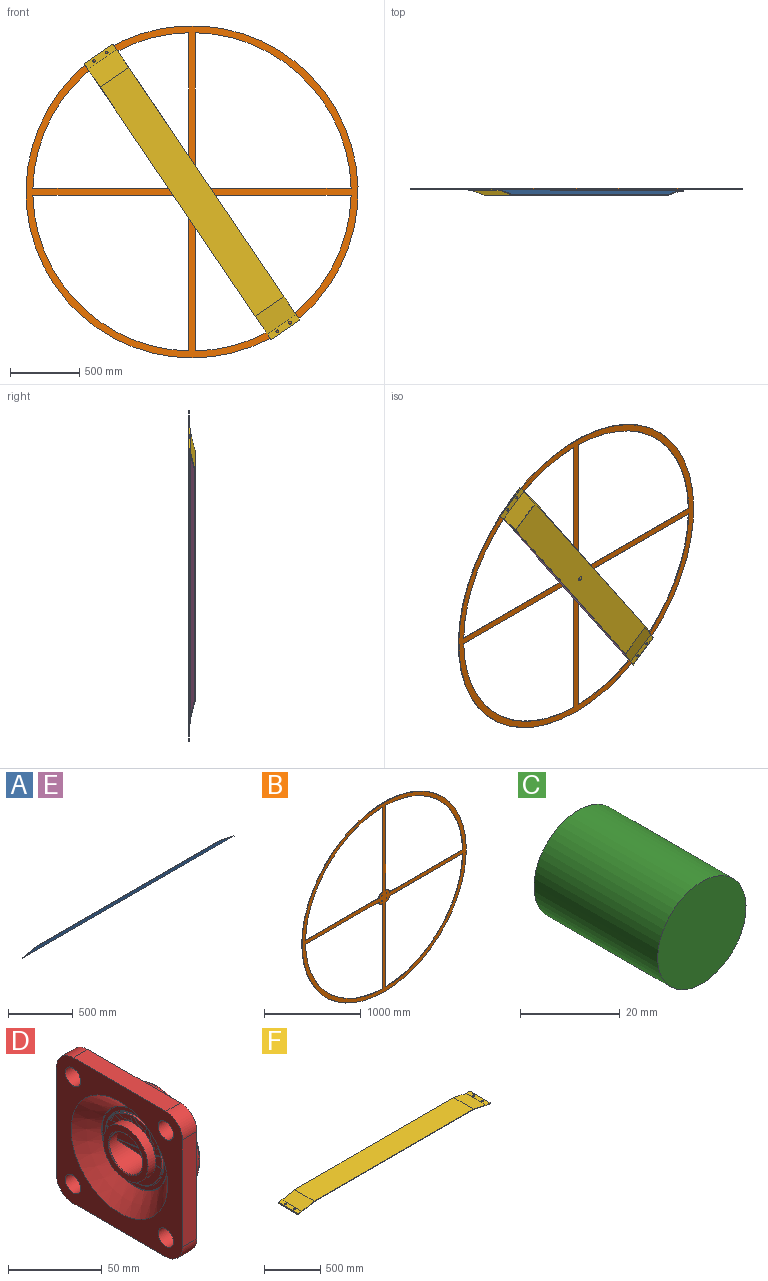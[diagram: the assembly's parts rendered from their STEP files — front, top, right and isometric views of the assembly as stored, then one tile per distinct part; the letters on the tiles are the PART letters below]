
ASSEMBLY  parts=6 mates=5
PART A: 6 faces, bbox 2310x5x33 mm
  f0: plane 155x33mm, normal (0.21,0,0.98), area 792.4mm2, adj f1,f3,f4,f5
  f1: plane 2000x5mm, normal (0,0,1), area 10000mm2, adj f0,f2,f4,f5
  f2: plane 155x33mm, normal (-0.21,0,0.98), area 792.4mm2, adj f1,f3,f4,f5
  f3: plane 2310x5mm, normal (0,0,-1), area 11550mm2, adj f0,f2,f4,f5
  f4: plane 2310x33mm, normal (0,-1,0), area 71115mm2, adj f0,f1,f2,f3
  f5: plane 2310x33mm, normal (0,1,0), area 71115mm2, adj f0,f1,f2,f3
PART B: 31 faces, bbox 2400x5x2400 mm
  f0: cylinder r=1150mm len=1124.73mm, axis (0,1,0), area 8782.1mm2, adj f1,f24,f29,f30
  f1: plane 1074.73x5mm, normal (1,0,0), area 5373.6mm2, adj f0,f2,f29,f30
  f2: plane 10.63x5mm, normal (0,0,-1), area 53.1mm2, adj f1,f3,f29,f30
  f3: cylinder r=45mm len=39.37mm, axis (0,1,0), area 300.2mm2, adj f2,f4,f29,f30
  f4: plane 10.63x5mm, normal (1,0,0), area 53.1mm2, adj f3,f24,f29,f30
  f5: plane 1074.73x5mm, normal (1,0,0), area 5373.6mm2, adj f6,f25,f29,f30
  f6: cylinder r=1150mm len=1124.73mm, axis (0,1,0), area 8782.1mm2, adj f5,f7,f29,f30
  f7: plane 1074.73x5mm, normal (0,0,1), area 5373.6mm2, adj f6,f8,f29,f30
  f8: plane 10.63x5mm, normal (1,0,0), area 53.1mm2, adj f7,f9,f29,f30
  f9: cylinder r=45mm len=39.37mm, axis (0,1,0), area 300.2mm2, adj f8,f25,f29,f30
  f10: plane 1074.73x5mm, normal (0,0,1), area 5373.6mm2, adj f11,f26,f29,f30
  f11: cylinder r=1150mm len=1124.73mm, axis (0,1,0), area 8782.1mm2, adj f10,f12,f29,f30
  f12: plane 1074.73x5mm, normal (-1,0,0), area 5373.6mm2, adj f11,f13,f29,f30
  f13: plane 10.63x5mm, normal (0,0,1), area 53.1mm2, adj f12,f14,f29,f30
  f14: cylinder r=45mm len=39.37mm, axis (0,1,0), area 300.2mm2, adj f13,f26,f29,f30
  f15: cylinder r=1150mm len=1124.73mm, axis (0,1,0), area 8782.1mm2, adj f16,f27,f29,f30
  f16: plane 1074.73x5mm, normal (0,0,-1), area 5373.6mm2, adj f15,f17,f29,f30
  f17: plane 10.63x5mm, normal (-1,0,0), area 53.1mm2, adj f16,f18,f29,f30
  f18: cylinder r=45mm len=39.37mm, axis (0,1,0), area 300.2mm2, adj f17,f19,f29,f30
  f19: plane 10.63x5mm, normal (0,0,-1), area 53.1mm2, adj f18,f27,f29,f30
  f20: cylinder r=5.5mm len=11mm, axis (0,1,0), area 172.8mm2, adj f29,f30
  f21: cylinder r=5.5mm len=11mm, axis (0,1,0), area 172.8mm2, adj f29,f30
  f22: cylinder r=5.5mm len=11mm, axis (0,1,0), area 172.8mm2, adj f29,f30
  f23: cylinder r=1200mm len=2400mm, axis (0,1,0), area 37699.1mm2, adj f29,f30
  f24: plane 1074.73x5mm, normal (0,0,-1), area 5373.6mm2, adj f0,f4,f29,f30
  f25: plane 10.63x5mm, normal (0,0,1), area 53.1mm2, adj f5,f9,f29,f30
  f26: plane 10.63x5mm, normal (-1,0,0), area 53.1mm2, adj f10,f14,f29,f30
  f27: plane 1074.73x5mm, normal (-1,0,0), area 5373.6mm2, adj f15,f19,f29,f30
  f28: cylinder r=5.5mm len=11mm, axis (0,1,0), area 172.8mm2, adj f29,f30
  f29: plane 2400x2400mm, normal (0,-1,0), area 604604.7mm2, adj f0,f1,f2,f3,f4,f5,f6,f7
  f30: plane 2400x2400mm, normal (0,1,0), area 604604.7mm2, adj f0,f1,f2,f3,f4,f5,f6,f7
PART C: 3 faces, bbox 25x35x25 mm
  f0: cylinder r=12.5mm len=35mm, axis (0,1,0), area 2748.9mm2, adj f1,f2
  f1: plane 25x25mm, normal (0,-1,0), area 490.9mm2, adj f0
  f2: plane 25x25mm, normal (0,1,0), area 490.9mm2, adj f0
PART D: 78 faces, bbox 52x95x95 mm
  f0: plane 2.89x2.17mm, normal (0,-0.5,0.87), area 5.4mm2, adj f2,f3,f4,f5,f6,f7
  f1: plane 2.89x2.5mm, normal (0,1,0), area 5.4mm2, adj f8,f9,f10,f11,f12,f13
  f2: plane 1.77x1.74mm, normal (0.87,0.43,0.25), area 1.9mm2, adj f0,f3,f7,f14
  f3: plane 1.44x1.14mm, normal (0,0.87,0.5), area 1.9mm2, adj f0,f2,f4,f14
  f4: plane 1.77x1.74mm, normal (-0.87,0.43,0.25), area 1.9mm2, adj f0,f3,f5,f14
  f5: plane 1.77x1.74mm, normal (-0.87,-0.43,-0.25), area 1.9mm2, adj f0,f4,f6,f14
  f6: plane 1.44x1.14mm, normal (0,-0.87,-0.5), area 1.9mm2, adj f0,f5,f7,f14
  f7: plane 1.77x1.74mm, normal (0.87,-0.43,-0.25), area 1.9mm2, adj f0,f2,f6,f14
  f8: plane 1.32x1.25mm, normal (0.5,0,0.87), area 1.9mm2, adj f1,f9,f13,f15
  f9: plane 1.44x1.32mm, normal (1,0,0), area 1.9mm2, adj f1,f8,f10,f15
  f10: plane 1.32x1.25mm, normal (0.5,0,-0.87), area 1.9mm2, adj f1,f9,f11,f15
  f11: plane 1.32x1.25mm, normal (-0.5,0,-0.87), area 1.9mm2, adj f1,f10,f12,f15
  f12: plane 1.44x1.32mm, normal (-1,0,0), area 1.9mm2, adj f1,f11,f13,f15
  f13: plane 1.32x1.25mm, normal (-0.5,0,0.87), area 1.9mm2, adj f1,f8,f12,f15
  f14: plane 5.09x4.33mm, normal (0,-0.5,0.87), area 14.2mm2, adj f2,f3,f4,f5,f6,f7,f16
  f15: plane 5.09x5mm, normal (0,1,0), area 14.2mm2, adj f8,f9,f10,f11,f12,f13,f17
  f16: cylinder r=2.5mm len=5mm, axis (0,0.5,-0.87), area 14.2mm2, adj f14,f18
  f17: cylinder r=2.5mm len=5mm, axis (0,-1,0), area 14.2mm2, adj f15,f18
  f18: cylinder r=16.9mm len=33.8mm, axis (-1,0,0), area 1176.5mm2, adj f16,f17,f19,f20
  f19: plane 43.29x42.5mm, normal (1,0,0), area 521.4mm2, adj f18,f21
  f20: plane 34.43x33.8mm, normal (1,0,0), area 366.3mm2, adj f18,f22
  f21: cylinder r=21.25mm len=42.5mm, axis (-1,0,0), area 166.9mm2, adj f19,f23
  f22: torus R=13mm, axis (-1,0,0), area 62.6mm2, adj f20,f24
  f23: plane 44.97x44.16mm, normal (1,0,0), area 112.7mm2, adj f21,f25
  f24: cylinder r=12.5mm len=33.1mm, axis (-1,0,0), area 2599.7mm2, adj f22,f26
  f25: cylinder r=22.08mm len=44.16mm, axis (-1,0,0), area 55.5mm2, adj f23,f27
  f26: torus R=13mm, axis (-1,0,0), area 62.6mm2, adj f24,f28
  f27: plane 49.5x49.04mm, normal (1,0,0), area 357.5mm2, adj f25,f29
  f28: plane 34.43x33.8mm, normal (-1,0,0), area 366.3mm2, adj f26,f30
  f29: torus R=24.52mm, axis (-1,0,0), area 100.7mm2, adj f27,f31
  f30: cylinder r=16.9mm len=33.8mm, axis (-1,0,0), area 631.8mm2, adj f28,f32
  f31: sphere r=26mm, area 64.7mm2, adj f29,f33
  f32: plane 43.29x42.5mm, normal (-1,0,0), area -733.9mm2, adj f30,f35
  f33: cone r=25.12mm half-angle=10deg, axis (1,0,0), area 402.3mm2, adj f31,f36
  f34: sphere r=26mm, area 0mm2, adj f37
  f35: cylinder r=21.25mm len=42.5mm, axis (-1,0,0), area 166.9mm2, adj f32,f38
  f36: plane 61.85x61.29mm, normal (1,0,0), area 932.4mm2, adj f33,f39
  f37: cylinder r=4.29mm len=10.68mm, axis (-0.26,-0.97,0), area 213.4mm2, adj f34,f40
  f38: plane 44.97x44.16mm, normal (-1,0,0), area -1650.4mm2, adj f35,f41
  f39: torus R=30.64mm, axis (-1,0,0), area 522.5mm2, adj f36,f40,f42
  f40: cone r=5.07mm half-angle=45deg, axis (0.26,0.97,0), area 17mm2, adj f37,f39,f42
  f41: cylinder r=22.08mm len=44.16mm, axis (-1,0,0), area 55.5mm2, adj f38,f43
  f42: cone r=34.59mm half-angle=15deg, axis (-1,0,0), area 3314mm2, adj f39,f40,f44
  f43: plane 49.5x49.04mm, normal (-1,0,0), area 357.5mm2, adj f41,f45
  f44: torus R=38.53mm, axis (-1,0,0), area 615.2mm2, adj f42,f46
  f45: torus R=24.52mm, axis (-1,0,0), area 100.7mm2, adj f43,f47
  f46: plane 95x95mm, normal (1,0,0), area 3810.4mm2, adj f44,f48,f49,f50,f51,f52,f53,f54
  f47: sphere r=26mm, area 59.3mm2, adj f45,f60
  f48: cylinder r=5.75mm len=11.5mm, axis (-1,0,0), area 397.4mm2, adj f46,f61
  f49: cylinder r=5.75mm len=11.5mm, axis (-1,0,0), area 397.4mm2, adj f46,f61
  f50: cylinder r=5.75mm len=11.5mm, axis (-1,0,0), area 397.4mm2, adj f46,f61
  f51: cylinder r=5.75mm len=11.5mm, axis (-1,0,0), area 397.4mm2, adj f46,f61
  f52: plane 70x11mm, normal (0,1,0), area 770mm2, adj f46,f53,f59,f61
  f53: cylinder r=12.5mm len=12.5mm, axis (-1,0,0), area 216mm2, adj f46,f52,f54,f61
  f54: plane 70x11mm, normal (0,0,-1), area 770mm2, adj f46,f53,f55,f61
  f55: cylinder r=12.5mm len=12.5mm, axis (-1,0,0), area 216mm2, adj f46,f54,f56,f61
  f56: plane 70x11mm, normal (0,-1,0), area 770mm2, adj f46,f55,f57,f61
  f57: cylinder r=12.5mm len=12.5mm, axis (-1,0,0), area 216mm2, adj f46,f56,f58,f61
  f58: plane 70x11mm, normal (0,0,1), area 770mm2, adj f46,f57,f59,f61
  f59: cylinder r=12.5mm len=12.5mm, axis (-1,0,0), area 216mm2, adj f46,f52,f58,f61
  f60: cone r=30.64mm half-angle=45deg, axis (-1,0,0), area 3131.5mm2, adj f47,f61
  f61: plane 95x95mm, normal (-1,0,0), area 4314.1mm2, adj f48,f49,f50,f51,f52,f53,f54,f55
  f62: sphere r=26mm, area 0mm2, adj f64
  f63: sphere r=26mm, area 0mm2, adj f65
  f64: cylinder r=0.5mm len=3.7mm, axis (0,-1,0), area 11.4mm2, adj f62,f67
  f65: cylinder r=0.5mm len=3.7mm, axis (0,-1,0), area 11.4mm2, adj f63,f67
  f66: torus R=19.3mm, axis (-1,0,0), area 907mm2, adj f67,f68
  f67: cylinder r=22.08mm len=44.16mm, axis (-1,0,0), area 520.3mm2, adj f64,f65,f66,f69
  f68: cylinder r=22.08mm len=44.16mm, axis (-1,0,0), area 453mm2, adj f66,f70
  f69: plane 44.78x44.57mm, normal (1,0,0), area 243.1mm2, adj f67,f71
  f70: plane 44.52x44.31mm, normal (-1,0,0), area 243.1mm2, adj f68,f72
  f71: cylinder r=20.25mm len=40.5mm, axis (-1,0,0), area 159mm2, adj f69,f73
  f72: cylinder r=20.25mm len=40.5mm, axis (-1,0,0), area 159mm2, adj f70,f74
  f73: plane 41.25x40.5mm, normal (1,0,0), area 391mm2, adj f71,f77
  f74: plane 41.25x40.5mm, normal (-1,0,0), area 391mm2, adj f72,f75
  f75: cylinder r=16.9mm len=33.8mm, axis (-1,0,0), area 444.8mm2, adj f74,f76
  f76: torus R=19.3mm, axis (-1,0,0), area 729.3mm2, adj f75,f77
  f77: cylinder r=16.9mm len=33.8mm, axis (-1,0,0), area 444.8mm2, adj f73,f76
PART E: same geometry as A
PART F: 22 faces, bbox 2410x250x46 mm
  f0: plane 250x45mm, normal (0,0,-1), area 10652.7mm2, adj f1,f15,f16,f17,f20,f21
  f1: plane 250x8mm, normal (-1,0,0), area 2000mm2, adj f0,f2,f16,f17
  f2: plane 250x5mm, normal (0,0,-1), area 1250mm2, adj f1,f3,f16,f17
  f3: plane 250x13mm, normal (1,0,0), area 3250mm2, adj f2,f4,f16,f17
  f4: plane 250x50mm, normal (0,0,1), area 11902.7mm2, adj f3,f5,f16,f17,f20,f21
  f5: plane 250x155mm, normal (0.21,0,0.98), area 39618.5mm2, adj f4,f6,f16,f17
  f6: plane 2000x250mm, normal (0,0,1), area 500000mm2, adj f5,f7,f16,f17
  f7: plane 250x155mm, normal (-0.21,0,0.98), area 39618.5mm2, adj f6,f8,f16,f17
  f8: plane 250x50mm, normal (0,0,1), area 11902.7mm2, adj f7,f9,f16,f17,f18,f19
  f9: plane 250x13mm, normal (-1,0,0), area 3250mm2, adj f8,f10,f16,f17
  f10: plane 250x5mm, normal (0,0,-1), area 1250mm2, adj f9,f11,f16,f17
  f11: plane 250x8mm, normal (1,0,0), area 2000mm2, adj f10,f12,f16,f17
  f12: plane 250x45mm, normal (0,0,-1), area 10652.7mm2, adj f11,f13,f16,f17,f18,f19
  f13: plane 250x155mm, normal (0.21,0,-0.98), area 39618.5mm2, adj f12,f14,f16,f17
  f14: plane 2000x250mm, normal (0,0,-1), area 500000mm2, adj f13,f15,f16,f17
  f15: plane 250x155mm, normal (-0.21,0,-0.98), area 39618.5mm2, adj f0,f14,f16,f17
  f16: plane 2410x46mm, normal (0,-1,0), area 12130mm2, adj f0,f1,f2,f3,f4,f5,f6,f7
  f17: plane 2410x46mm, normal (0,1,0), area 12130mm2, adj f0,f1,f2,f3,f4,f5,f6,f7
  f18: cylinder r=9.75mm len=19.5mm, axis (0,0,1), area 306.3mm2, adj f8,f12
  f19: cylinder r=9.75mm len=19.5mm, axis (0,0,1), area 306.3mm2, adj f8,f12
  f20: cylinder r=9.75mm len=19.5mm, axis (0,0,1), area 306.3mm2, adj f0,f4
  f21: cylinder r=9.75mm len=19.5mm, axis (0,0,1), area 306.3mm2, adj f0,f4
PLACE A rot(axis=(0.8,0.42,-0.42),102.7deg) t=(-366.72,168.77,671.39)mm
PLACE B t=(-470.19,198.07,601.25)mm fixed
PLACE C rot(axis=(0,1,0),55.9deg) t=(-470.19,172.27,601.25)mm
PLACE D rot(axis=(-0.58,0.58,-0.58),120deg) t=(-470.19,174.07,601.25)mm
PLACE E rot(axis=(0.8,0.42,-0.42),102.7deg) t=(-569.52,168.77,533.92)mm
PLACE F rot(axis=(0.8,0.42,-0.42),102.7deg) t=(-366.72,168.77,671.39)mm
MATE revolute F.f14 <-> D.f24  axis (0,1,0) through (-470.19,154.77,601.25)mm
MATE fastened D.f24 <-> B.f23  axis (0,1,0) through (-470.19,193.07,601.25)mm
MATE fastened C.f0 <-> F.f14  axis (0,-1,0) through (-470.19,154.77,601.25)mm
MATE fastened A.f5 <-> F.f17  axis (0.83,0,0.56) through (-366.72,154.77,671.39)mm
MATE fastened E.f4 <-> F.f16  axis (-0.83,0,-0.56) through (-573.66,154.77,531.12)mm
